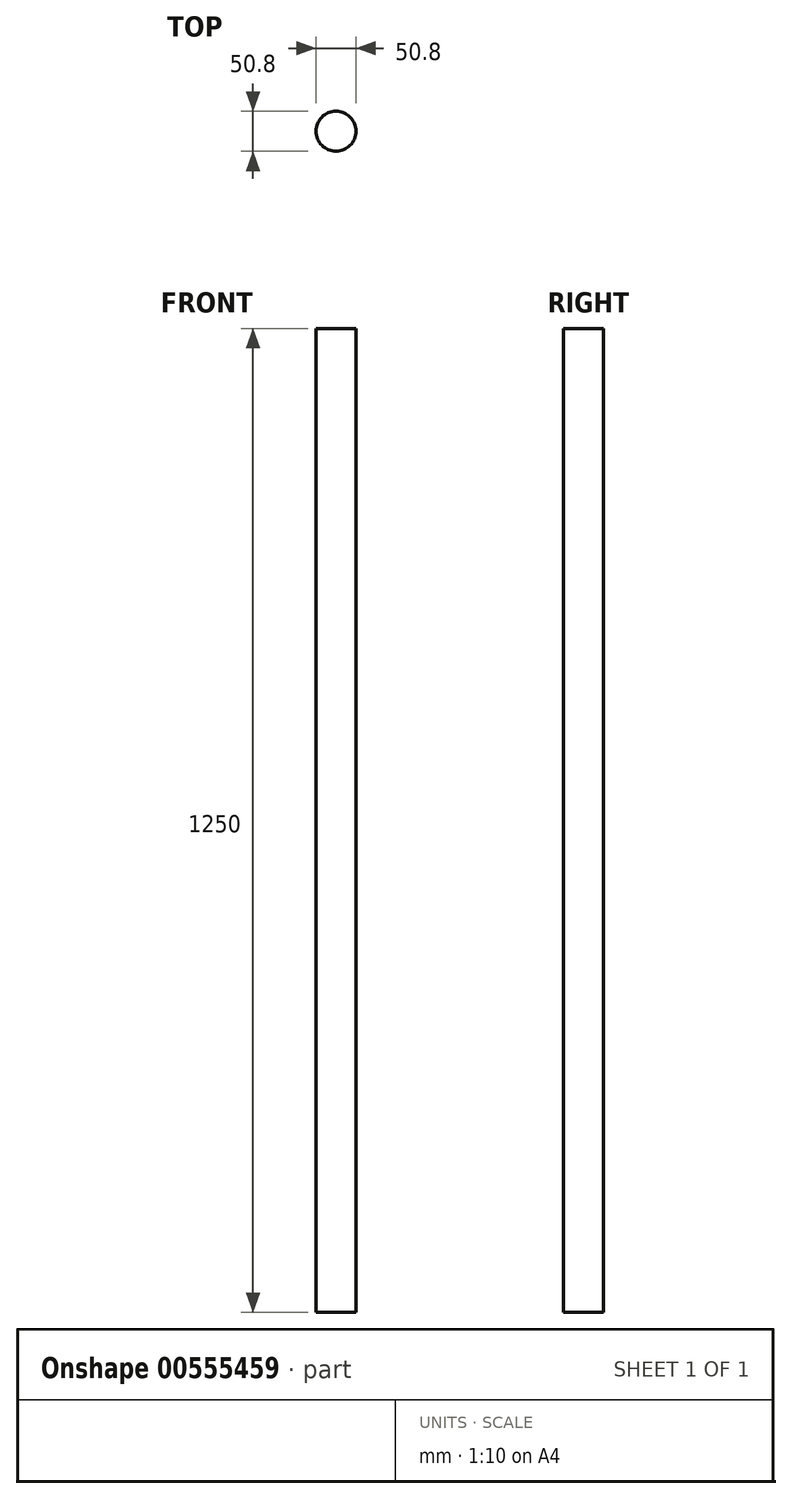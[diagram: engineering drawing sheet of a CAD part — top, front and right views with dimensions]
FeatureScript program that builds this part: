
annotation { "Feature Type Name" : "Feature", "Feature Type Description" : "" }
export const myFeature = defineFeature(function(context is Context, id is Id, definition is map)
    precondition{}
    {
        {
            var Q0;
            Q0=qCreatedBy(makeId("Top.planeOp"),FACE);
            var sketch = newSketch(context, id + "F0", { "sketchPlane" : qUnion([Q0])});
            skCircle(sketch, "E0", {"center": v(0, 0) * mm, "radius": 25.4 * mm});
            skSolve(sketch);
        }
        {
            var Q0;
            Q0=qSketchRegion(id+"F0",true);
            extrude(context, id + "F1", {"entities" : qUnion([Q0]), "depth" : 1250 * mm, "offsetDistance" : 25.4 * mm});
        }
    });
